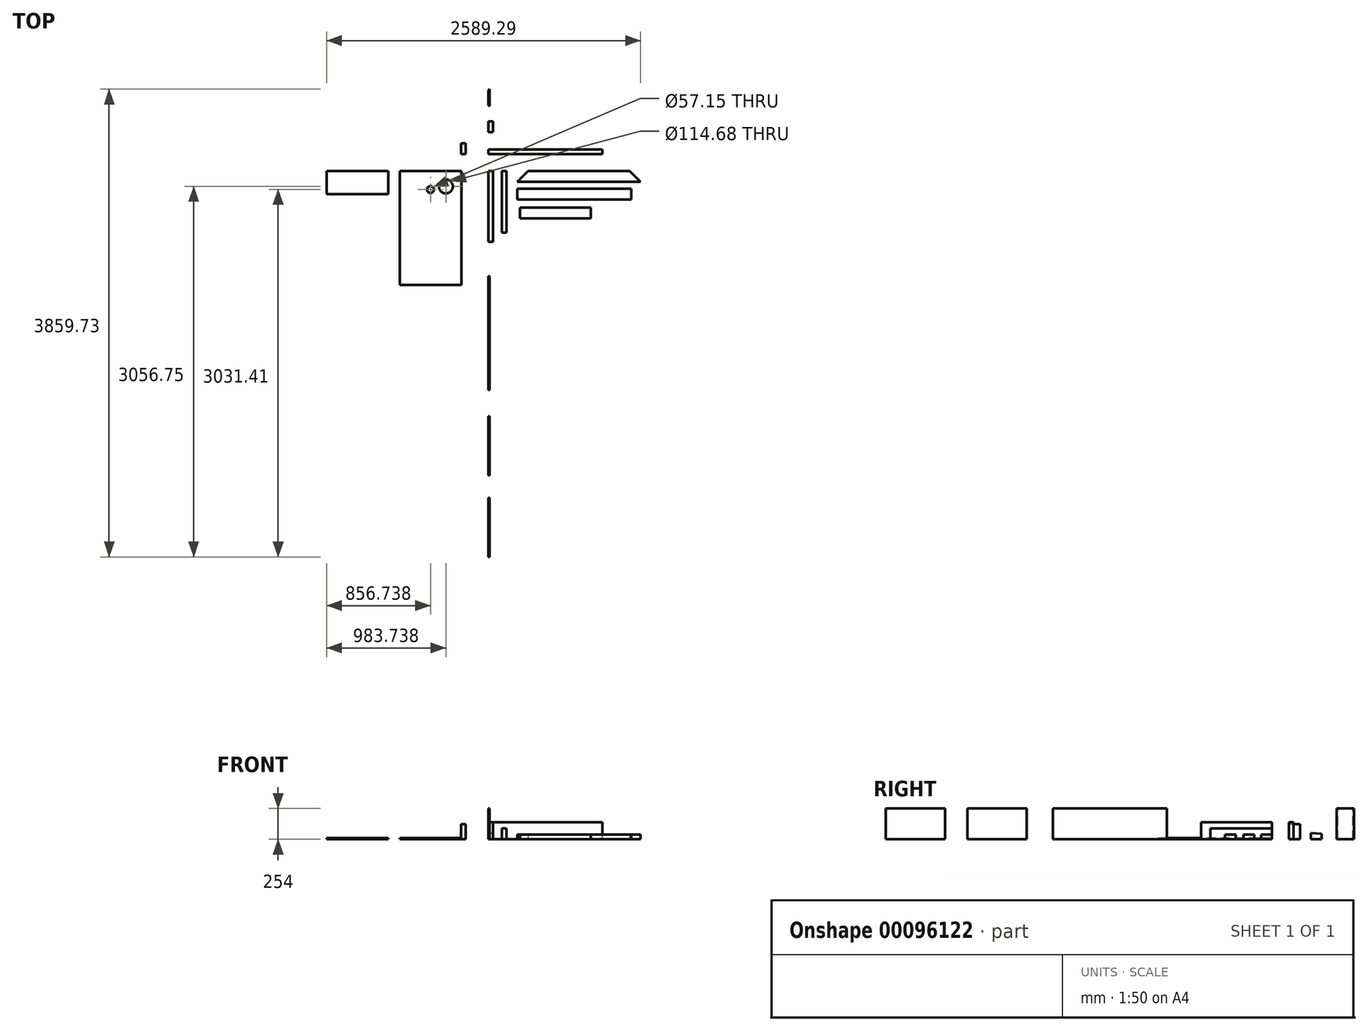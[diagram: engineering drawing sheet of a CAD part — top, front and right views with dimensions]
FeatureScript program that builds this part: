
annotation { "Feature Type Name" : "Feature", "Feature Type Description" : "" }
export const myFeature = defineFeature(function(context is Context, id is Id, definition is map)
    precondition{}
    {
        {
            var Q0;
            Q0=qCreatedBy(makeId("Front.planeOp"),FACE);
            var sketch = newSketch(context, id + "F0", { "sketchPlane" : qUnion([Q0])});
            skLineSegment(sketch, "E0.bottom", {"start": v(0, 0) * mm, "end": v(38.1, 0) * mm});
            skLineSegment(sketch, "E0.top", {"start": v(0, 139.7) * mm, "end": v(38.1, 139.7) * mm});
            skLineSegment(sketch, "E0.left", {"start": v(0, 0) * mm, "end": v(0, 139.7) * mm});
            skLineSegment(sketch, "E0.right", {"start": v(38.1, 0) * mm, "end": v(38.1, 139.7) * mm});
            skSolve(sketch);
        }
        {
            var Q0;
            Q0=makeQuery(id+"F0.imprint","IMPRINT",FACE,{"disambiguationData":[TD([[makeQuery(id+"F0.imprint","IMPRINT",EDGE,{"derivedFrom":sQuery(id+"F0.wireOp",EDGE,"E0.bottom")}),1.0]])]});
            extrude(context, id + "F1", {"entities" : qUnion([Q0]), "depth" : 584.2 * mm});
        }
        {
            var Q0;
            Q0=qCreatedBy(makeId("Right.planeOp"),FACE);
            var sketch = newSketch(context, id + "F2", { "sketchPlane" : qUnion([Q0])});
            skLineSegment(sketch, "E1.bottom", {"start": v(138.59, 0) * mm, "end": v(176.69, 0) * mm});
            skLineSegment(sketch, "E1.top", {"start": v(138.59, 139.7) * mm, "end": v(176.69, 139.7) * mm});
            skLineSegment(sketch, "E1.left", {"start": v(138.59, 0) * mm, "end": v(138.59, 139.7) * mm});
            skLineSegment(sketch, "E1.right", {"start": v(176.69, 0) * mm, "end": v(176.69, 139.7) * mm});
            skSolve(sketch);
        }
        {
            var Q0;
            Q0=makeQuery(id+"F2.imprint","IMPRINT",FACE,{"disambiguationData":[TD([[makeQuery(id+"F2.imprint","IMPRINT",EDGE,{"derivedFrom":sQuery(id+"F2.wireOp",EDGE,"E1.bottom")}),1.0]])]});
            extrude(context, id + "F3", {"entities" : qUnion([Q0]), "depth" : 939.8 * mm});
        }
        {
            var Q0;
            Q0=qCreatedBy(makeId("Front.planeOp"),FACE);
            var sketch = newSketch(context, id + "F4", { "sketchPlane" : qUnion([Q0])});
            skLineSegment(sketch, "E2.bottom", {"start": v(110.06, 0) * mm, "end": v(148.16, 0) * mm});
            skLineSegment(sketch, "E2.top", {"start": v(110.06, 88.9) * mm, "end": v(148.16, 88.9) * mm});
            skLineSegment(sketch, "E2.left", {"start": v(110.06, 0) * mm, "end": v(110.06, 88.9) * mm});
            skLineSegment(sketch, "E2.right", {"start": v(148.16, 0) * mm, "end": v(148.16, 88.9) * mm});
            skSolve(sketch);
        }
        {
            var Q0;
            Q0=makeQuery(id+"F4.imprint","IMPRINT",FACE,{"disambiguationData":[TD([[makeQuery(id+"F4.imprint","IMPRINT",EDGE,{"derivedFrom":sQuery(id+"F4.wireOp",EDGE,"E2.bottom")}),1.0]])]});
            extrude(context, id + "F5", {"entities" : qUnion([Q0]), "depth" : 508 * mm});
        }
        {
            var Q0;
            Q0=qCreatedBy(makeId("Top.planeOp"),FACE);
            var sketch = newSketch(context, id + "F6", { "sketchPlane" : qUnion([Q0])});
            skLineSegment(sketch, "E3.bottom", {"start": v(-224.08, 0) * mm, "end": v(-732.08, 0) * mm});
            skLineSegment(sketch, "E3.top", {"start": v(-224.08, -939.8) * mm, "end": v(-732.08, -939.8) * mm});
            skLineSegment(sketch, "E3.left", {"start": v(-224.08, 0) * mm, "end": v(-224.08, -939.8) * mm});
            skLineSegment(sketch, "E3.right", {"start": v(-732.08, 0) * mm, "end": v(-732.08, -939.8) * mm});
            skSolve(sketch);
        }
        {
            var Q0;
            Q0=makeQuery(id+"F6.imprint","IMPRINT",FACE,{"disambiguationData":[TD([[makeQuery(id+"F6.imprint","IMPRINT",EDGE,{"derivedFrom":sQuery(id+"F6.wireOp",EDGE,"E3.bottom")}),1.0]])]});
            extrude(context, id + "F7", {"entities" : qUnion([Q0]), "depth" : 9.52 * mm});
        }
        {
            var Q0;
            Q0=qCreatedBy(makeId("Top.planeOp"),FACE);
            var sketch = newSketch(context, id + "F8", { "sketchPlane" : qUnion([Q0])});
            skLineSegment(sketch, "E4.bottom", {"start": v(-826.82, 0) * mm, "end": v(-1334.82, 0) * mm});
            skLineSegment(sketch, "E4.top", {"start": v(-826.82, -190.5) * mm, "end": v(-1334.82, -190.5) * mm});
            skLineSegment(sketch, "E4.left", {"start": v(-826.82, 0) * mm, "end": v(-826.82, -190.5) * mm});
            skLineSegment(sketch, "E4.right", {"start": v(-1334.82, 0) * mm, "end": v(-1334.82, -190.5) * mm});
            skSolve(sketch);
        }
        {
            var Q0;
            Q0=makeQuery(id+"F8.imprint","IMPRINT",FACE,{"disambiguationData":[TD([[makeQuery(id+"F8.imprint","IMPRINT",EDGE,{"derivedFrom":sQuery(id+"F8.wireOp",EDGE,"E4.bottom")}),1.0]])]});
            extrude(context, id + "F9", {"entities" : qUnion([Q0]), "depth" : 9.52 * mm});
        }
        {
            var Q0;
            Q0=qCreatedBy(makeId("Right.planeOp"),FACE);
            var sketch = newSketch(context, id + "F10", { "sketchPlane" : qUnion([Q0])});
            skLineSegment(sketch, "E5", {"start": v(-866.98, 0) * mm, "end": v(-866.98, 254) * mm});
            skLineSegment(sketch, "E6", {"start": v(-866.98, 254) * mm, "end": v(-1806.78, 254) * mm});
            skLineSegment(sketch, "E7", {"start": v(-1806.78, 254) * mm, "end": v(-1806.78, 0) * mm});
            skLineSegment(sketch, "E8", {"start": v(-1806.78, 0) * mm, "end": v(-1616.28, 0) * mm});
            skLineSegment(sketch, "E9", {"start": v(-1616.28, 0) * mm, "end": v(-1616.28, 0) * mm});
            skLineSegment(sketch, "E10", {"start": v(-1616.28, 0) * mm, "end": v(-866.98, 0) * mm});
            skSolve(sketch);
        }
        {
            var Q0;
            Q0=makeQuery(id+"F10.imprint","IMPRINT",FACE,{"disambiguationData":[TD([[makeQuery(id+"F10.imprint","IMPRINT",EDGE,{"derivedFrom":sQuery(id+"F10.wireOp",EDGE,"E5")}),1.0]])]});
            extrude(context, id + "F11", {"entities" : qUnion([Q0]), "depth" : 9.52 * mm});
        }
        {
            var Q0;
            Q0=qCreatedBy(makeId("Right.planeOp"),FACE);
            var sketch = newSketch(context, id + "F12", { "sketchPlane" : qUnion([Q0])});
            skLineSegment(sketch, "E11.bottom", {"start": v(-2022.5, 0) * mm, "end": v(-2511.45, 0) * mm});
            skLineSegment(sketch, "E11.top", {"start": v(-2022.5, 254) * mm, "end": v(-2511.45, 254) * mm});
            skLineSegment(sketch, "E11.left", {"start": v(-2022.5, 0) * mm, "end": v(-2022.5, 254) * mm});
            skLineSegment(sketch, "E11.right", {"start": v(-2511.45, 0) * mm, "end": v(-2511.45, 254) * mm});
            skSolve(sketch);
        }
        {
            var Q0;
            Q0=makeQuery(id+"F12.imprint","IMPRINT",FACE,{"disambiguationData":[TD([[makeQuery(id+"F12.imprint","IMPRINT",EDGE,{"derivedFrom":sQuery(id+"F12.wireOp",EDGE,"E11.bottom")}),-1.0]])]});
            extrude(context, id + "F13", {"entities" : qUnion([Q0]), "depth" : 9.52 * mm});
        }
        {
            var Q0;
            Q0=qCreatedBy(makeId("Right.planeOp"),FACE);
            var sketch = newSketch(context, id + "F14", { "sketchPlane" : qUnion([Q0])});
            skLineSegment(sketch, "E12.bottom", {"start": v(-2694.8, 0) * mm, "end": v(-3183.75, 0) * mm});
            skLineSegment(sketch, "E12.top", {"start": v(-2694.8, 254) * mm, "end": v(-3183.75, 254) * mm});
            skLineSegment(sketch, "E12.left", {"start": v(-2694.8, 0) * mm, "end": v(-2694.8, 254) * mm});
            skLineSegment(sketch, "E12.right", {"start": v(-3183.75, 0) * mm, "end": v(-3183.75, 254) * mm});
            skSolve(sketch);
        }
        {
            var Q0;
            Q0=makeQuery(id+"F14.imprint","IMPRINT",FACE,{"disambiguationData":[TD([[makeQuery(id+"F14.imprint","IMPRINT",EDGE,{"derivedFrom":sQuery(id+"F14.wireOp",EDGE,"E12.bottom")}),-1.0]])]});
            extrude(context, id + "F15", {"entities" : qUnion([Q0]), "depth" : 9.52 * mm});
        }
        {
            var Q0;
            Q0=qCreatedBy(makeId("Top.planeOp"),FACE);
            var sketch = newSketch(context, id + "F16", { "sketchPlane" : qUnion([Q0])});
            skLineSegment(sketch, "E13.bottom", {"start": v(327.37, 0) * mm, "end": v(1165.57, 0) * mm});
            skLineSegment(sketch, "E13.top", {"start": v(238.47, -88.9) * mm, "end": v(1254.47, -88.9) * mm});
            skLineSegment(sketch, "E14", {"start": v(238.47, -88.9) * mm, "end": v(327.37, 0) * mm});
            skLineSegment(sketch, "E15", {"start": v(1254.47, -88.9) * mm, "end": v(1165.57, 0) * mm});
            skSolve(sketch);
        }
        {
            var Q0;
            Q0=makeQuery(id+"F16.imprint","IMPRINT",FACE,{"disambiguationData":[TD([[makeQuery(id+"F16.imprint","IMPRINT",EDGE,{"derivedFrom":sQuery(id+"F16.wireOp",EDGE,"E13.bottom")}),-1.0]])]});
            extrude(context, id + "F17", {"entities" : qUnion([Q0]), "depth" : 38.1 * mm});
        }
        {
            var Q0;
            Q0=qCreatedBy(makeId("Top.planeOp"),FACE);
            var sketch = newSketch(context, id + "F18", { "sketchPlane" : qUnion([Q0])});
            skLineSegment(sketch, "E16.bottom", {"start": v(238.93, -146.3) * mm, "end": v(1178.73, -146.3) * mm});
            skLineSegment(sketch, "E16.top", {"start": v(238.93, -235.2) * mm, "end": v(1178.73, -235.2) * mm});
            skLineSegment(sketch, "E16.left", {"start": v(238.93, -146.3) * mm, "end": v(238.93, -235.2) * mm});
            skLineSegment(sketch, "E16.right", {"start": v(1178.73, -146.3) * mm, "end": v(1178.73, -235.2) * mm});
            skSolve(sketch);
        }
        {
            var Q0;
            Q0=makeQuery(id+"F18.imprint","IMPRINT",FACE,{"disambiguationData":[TD([[makeQuery(id+"F18.imprint","IMPRINT",EDGE,{"derivedFrom":sQuery(id+"F18.wireOp",EDGE,"E16.bottom")}),-1.0]])]});
            extrude(context, id + "F19", {"entities" : qUnion([Q0]), "depth" : 38.1 * mm});
        }
        {
            var Q0;
            Q0=qCreatedBy(makeId("Top.planeOp"),FACE);
            var sketch = newSketch(context, id + "F20", { "sketchPlane" : qUnion([Q0])});
            skLineSegment(sketch, "E17.bottom", {"start": v(260.45, -300.02) * mm, "end": v(844.65, -300.02) * mm});
            skLineSegment(sketch, "E17.top", {"start": v(260.45, -388.92) * mm, "end": v(844.65, -388.92) * mm});
            skLineSegment(sketch, "E17.left", {"start": v(260.45, -300.02) * mm, "end": v(260.45, -388.92) * mm});
            skLineSegment(sketch, "E17.right", {"start": v(844.65, -300.02) * mm, "end": v(844.65, -388.92) * mm});
            skSolve(sketch);
        }
        {
            var Q0;
            Q0=makeQuery(id+"F20.imprint","IMPRINT",FACE,{"disambiguationData":[TD([[makeQuery(id+"F20.imprint","IMPRINT",EDGE,{"derivedFrom":sQuery(id+"F20.wireOp",EDGE,"E17.bottom")}),-1.0]])]});
            extrude(context, id + "F21", {"entities" : qUnion([Q0]), "depth" : 38.1 * mm});
        }
        {
            var Q0;
            Q0=qCreatedBy(makeId("Top.planeOp"),FACE);
            var sketch = newSketch(context, id + "F22", { "sketchPlane" : qUnion([Q0])});
            skLineSegment(sketch, "E18.bottom", {"start": v(-225.09, 141) * mm, "end": v(-186.99, 141) * mm});
            skLineSegment(sketch, "E18.top", {"start": v(-225.09, 229.9) * mm, "end": v(-186.99, 229.9) * mm});
            skLineSegment(sketch, "E18.left", {"start": v(-225.09, 141) * mm, "end": v(-225.09, 229.9) * mm});
            skLineSegment(sketch, "E18.right", {"start": v(-186.99, 141) * mm, "end": v(-186.99, 229.9) * mm});
            skSolve(sketch);
        }
        {
            var Q0;
            Q0=makeQuery(id+"F22.imprint","IMPRINT",FACE,{"disambiguationData":[TD([[makeQuery(id+"F22.imprint","IMPRINT",EDGE,{"derivedFrom":sQuery(id+"F22.wireOp",EDGE,"E18.bottom")}),1.0]])]});
            extrude(context, id + "F23", {"entities" : qUnion([Q0]), "depth" : 123.82 * mm});
        }
        {
            var Q0;
            Q0=qCreatedBy(makeId("Right.planeOp"),FACE);
            var sketch = newSketch(context, id + "F24", { "sketchPlane" : qUnion([Q0])});
            skLineSegment(sketch, "E19", {"start": v(320.73, 0) * mm, "end": v(320.73, 50.8) * mm});
            skLineSegment(sketch, "E20", {"start": v(320.73, 50.8) * mm, "end": v(409.63, 47.07) * mm});
            skLineSegment(sketch, "E21", {"start": v(409.63, 47.07) * mm, "end": v(409.63, 0) * mm});
            skLineSegment(sketch, "E22", {"start": v(409.63, 0) * mm, "end": v(320.73, 0) * mm});
            skSolve(sketch);
        }
        {
            var Q0;
            Q0=makeQuery(id+"F24.imprint","IMPRINT",FACE,{"disambiguationData":[TD([[makeQuery(id+"F24.imprint","IMPRINT",EDGE,{"derivedFrom":sQuery(id+"F24.wireOp",EDGE,"E19")}),-1.0]])]});
            extrude(context, id + "F25", {"entities" : qUnion([Q0]), "depth" : 38.1 * mm});
        }
        {
            var Q0;
            Q0=qCreatedBy(makeId("Right.planeOp"),FACE);
            var sketch = newSketch(context, id + "F26", { "sketchPlane" : qUnion([Q0])});
            skLineSegment(sketch, "E23.bottom", {"start": v(532.29, 0) * mm, "end": v(675.98, 0) * mm});
            skLineSegment(sketch, "E23.top", {"start": v(532.29, 254) * mm, "end": v(675.98, 254) * mm});
            skLineSegment(sketch, "E23.left", {"start": v(532.29, 0) * mm, "end": v(532.29, 254) * mm});
            skLineSegment(sketch, "E23.right", {"start": v(675.98, 0) * mm, "end": v(675.98, 254) * mm});
            skSolve(sketch);
        }
        {
            var Q0;
            Q0=makeQuery(id+"F26.imprint","IMPRINT",FACE,{"disambiguationData":[TD([[makeQuery(id+"F26.imprint","IMPRINT",EDGE,{"derivedFrom":sQuery(id+"F26.wireOp",EDGE,"E23.bottom")}),1.0]])]});
            extrude(context, id + "F27", {"entities" : qUnion([Q0]), "depth" : 9.52 * mm});
        }
        {
            var Q0;
            Q0=makeQuery(id+"F27.opExtrude","SWEPT_FACE",FACE,{"disambiguationData":[OSD([sQuery(id+"F26.wireOp",EDGE,"E23.top")])]});
            var sketch = newSketch(context, id + "F28", { "sketchPlane" : qUnion([Q0])});
            skLineSegment(sketch, "E24", {"start": v(9.53, 675.98) * mm, "end": v(0, 666.45) * mm});
            skLineSegment(sketch, "E25", {"start": v(0, 666.45) * mm, "end": v(0, 675.98) * mm});
            skLineSegment(sketch, "E26", {"start": v(0, 675.98) * mm, "end": v(9.53, 675.98) * mm});
            skLineSegment(sketch, "E27", {"start": v(9.52, 532.29) * mm, "end": v(0, 541.81) * mm});
            skLineSegment(sketch, "E28", {"start": v(0, 541.81) * mm, "end": v(0, 532.29) * mm});
            skLineSegment(sketch, "E29", {"start": v(0, 532.29) * mm, "end": v(9.53, 532.29) * mm});
            skSolve(sketch);
        }
        {
            var Q0;
            Q0=makeQuery(id+"F28.imprint","IMPRINT",FACE,{"disambiguationData":[TD([[makeQuery(id+"F28.imprint","IMPRINT",EDGE,{"derivedFrom":sQuery(id+"F28.wireOp",EDGE,"E24")}),-1.0]])]});
            var Q1;
            Q1=makeQuery(id+"F28.imprint","IMPRINT",FACE,{"disambiguationData":[TD([[makeQuery(id+"F28.imprint","IMPRINT",EDGE,{"derivedFrom":sQuery(id+"F28.wireOp",EDGE,"E27")}),1.0]])]});
            extrude(context, id + "F29", {"entities" : qUnion([Q0, Q1]), "operationType" : NewBodyOperationType.REMOVE, "oppositeDirection" : true, "depth" : 254 * mm});
        }
        {
            var Q0;
            Q0=makeQuery(id+"F7.opExtrude","CAP_EDGE",EDGE,{"disambiguationData":[OSD([sQuery(id+"F6.wireOp",EDGE,"E3.top")])],"isStart":false});
            cPlane(context, id + "F30", {"entities" : qUnion([Q0]), "cplaneType" : CPlaneType.LINE_ANGLE, "offset" : 152.4 * mm, "angle" : 87.6 * degree, "width" : 152.4 * mm, "height" : 152.4 * mm});
        }
        {
            var Q0;
            Q0=qCreatedBy(id+"F30.planeOp",FACE);
            var sketch = newSketch(context, id + "F31", { "sketchPlane" : qUnion([Q0])});
            skCircle(sketch, "E30", {"center": v(-478.08, -152) * mm, "radius": 28.58 * mm});
            skSolve(sketch);
        }
        {
            var Q0;
            Q0=makeQuery(id+"F31.imprint","IMPRINT",FACE,{"disambiguationData":[TD([[makeQuery(id+"F31.imprint","IMPRINT",EDGE,{"derivedFrom":sQuery(id+"F31.wireOp",EDGE,"E30")}),1.0]])]});
            extrude(context, id + "F32", {"entities" : qUnion([Q0]), "operationType" : NewBodyOperationType.REMOVE, "oppositeDirection" : true, "depth" : 76.2 * mm});
        }
        {
            var Q0;
            Q0=makeQuery(id+"F7.opExtrude","CAP_FACE",FACE,{"disambiguationData":[OSD([sQuery(id+"F6.wireOp",EDGE,"E3.bottom"),sQuery(id+"F6.wireOp",EDGE,"E3.top"),sQuery(id+"F6.wireOp",EDGE,"E3.left"),sQuery(id+"F6.wireOp",EDGE,"E3.right")])],"isStart":false});
            var sketch = newSketch(context, id + "F33", { "sketchPlane" : qUnion([Q0])});
            skCircle(sketch, "E31", {"center": v(-351.08, -127) * mm, "radius": 57.34 * mm});
            skSolve(sketch);
        }
        {
            var Q0;
            Q0=makeQuery(id+"F33.imprint","IMPRINT",FACE,{"disambiguationData":[TD([[makeQuery(id+"F33.imprint","IMPRINT",EDGE,{"derivedFrom":sQuery(id+"F33.wireOp",EDGE,"E31")}),1.0]])]});
            extrude(context, id + "F34", {"entities" : qUnion([Q0]), "operationType" : NewBodyOperationType.REMOVE, "oppositeDirection" : true, "depth" : 25.4 * mm});
        }
    });
